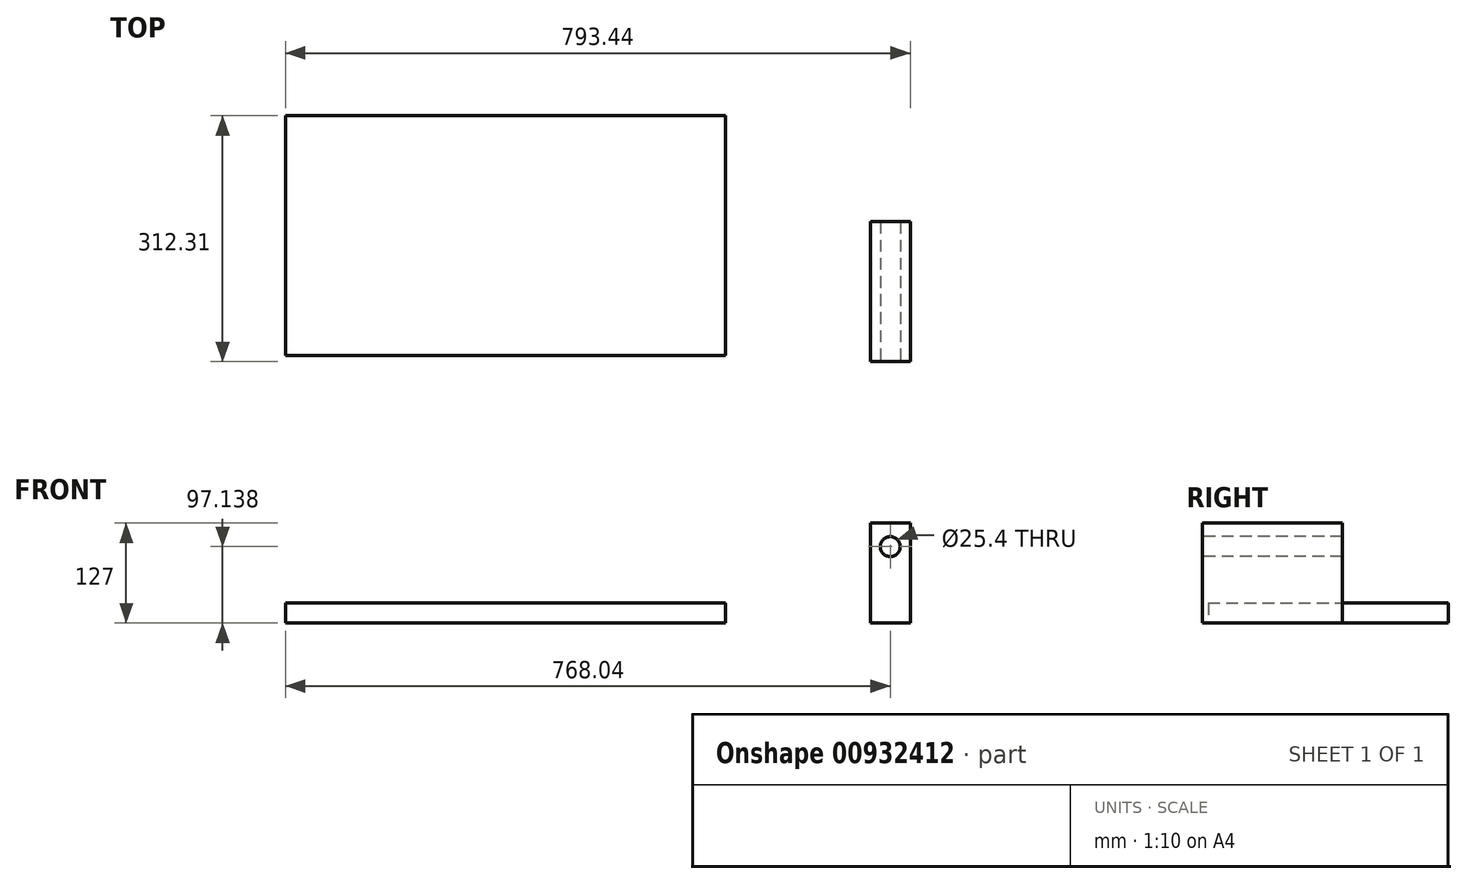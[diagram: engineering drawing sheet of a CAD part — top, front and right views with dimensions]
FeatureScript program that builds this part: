
annotation { "Feature Type Name" : "Feature", "Feature Type Description" : "" }
export const myFeature = defineFeature(function(context is Context, id is Id, definition is map)
    precondition{}
    {
        {
            var Q0;
            Q0=qCreatedBy(makeId("Top.planeOp"),FACE);
            var sketch = newSketch(context, id + "F0", { "sketchPlane" : qUnion([Q0])});
            skLineSegment(sketch, "E0.bottom", {"start": v(0, 0) * mm, "end": v(-558.8, 0) * mm});
            skLineSegment(sketch, "E0.top", {"start": v(0, 304.8) * mm, "end": v(-558.8, 304.8) * mm});
            skLineSegment(sketch, "E0.left", {"start": v(0, 0) * mm, "end": v(0, 304.8) * mm});
            skLineSegment(sketch, "E0.right", {"start": v(-558.8, 0) * mm, "end": v(-558.8, 304.8) * mm});
            skLineSegment(sketch, "E1.bottom", {"start": v(183.84, 170.29) * mm, "end": v(234.64, 170.29) * mm});
            skLineSegment(sketch, "E1.top", {"start": v(183.84, -7.51) * mm, "end": v(234.64, -7.51) * mm});
            skLineSegment(sketch, "E1.left", {"start": v(183.84, 170.29) * mm, "end": v(183.84, -7.51) * mm});
            skLineSegment(sketch, "E1.right", {"start": v(234.64, 170.29) * mm, "end": v(234.64, -7.51) * mm});
            skSolve(sketch);
        }
        {
            var Q0;
            Q0=makeQuery(id+"F0.imprint","IMPRINT",FACE,{"disambiguationData":[TD([[makeQuery(id+"F0.imprint","IMPRINT",EDGE,{"derivedFrom":sQuery(id+"F0.wireOp",EDGE,"E1.bottom")}),-1.0]])]});
            extrude(context, id + "F1", {"entities" : qUnion([Q0]), "depth" : 127 * mm, "offsetDistance" : 25.4 * mm});
        }
        {
            var Q0;
            Q0=makeQuery(id+"F0.imprint","IMPRINT",FACE,{"disambiguationData":[TD([[makeQuery(id+"F0.imprint","IMPRINT",EDGE,{"derivedFrom":sQuery(id+"F0.wireOp",EDGE,"E0.bottom")}),-1.0]])]});
            extrude(context, id + "F2", {"entities" : qUnion([Q0]), "depth" : 25.4 * mm, "offsetDistance" : 25.4 * mm});
        }
        {
            var Q0;
            Q0=makeQuery(id+"F1.opExtrude","SWEPT_FACE",FACE,{"disambiguationData":[OSD([sQuery(id+"F0.wireOp",EDGE,"E1.top")])]});
            var sketch = newSketch(context, id + "F3", { "sketchPlane" : qUnion([Q0])});
            skCircle(sketch, "E2", {"center": v(209.24, 97.14) * mm, "radius": 12.7 * mm});
            skPoint(sketch, "E2.centerSnap0", {"position": v(209.24, 127) * mm});
            skSolve(sketch);
        }
        {
            var Q0;
            Q0=makeQuery(id+"F3.imprint","IMPRINT",FACE,{"disambiguationData":[TD([[makeQuery(id+"F3.imprint","IMPRINT",EDGE,{"derivedFrom":sQuery(id+"F3.wireOp",EDGE,"E2")}),1.0]])]});
            extrude(context, id + "F4", {"entities" : qUnion([Q0]), "operationType" : NewBodyOperationType.REMOVE, "endBound" : BoundingType.UP_TO_NEXT, "oppositeDirection" : true, "depth" : 25.4 * mm, "offsetDistance" : 25.4 * mm});
        }
    });
